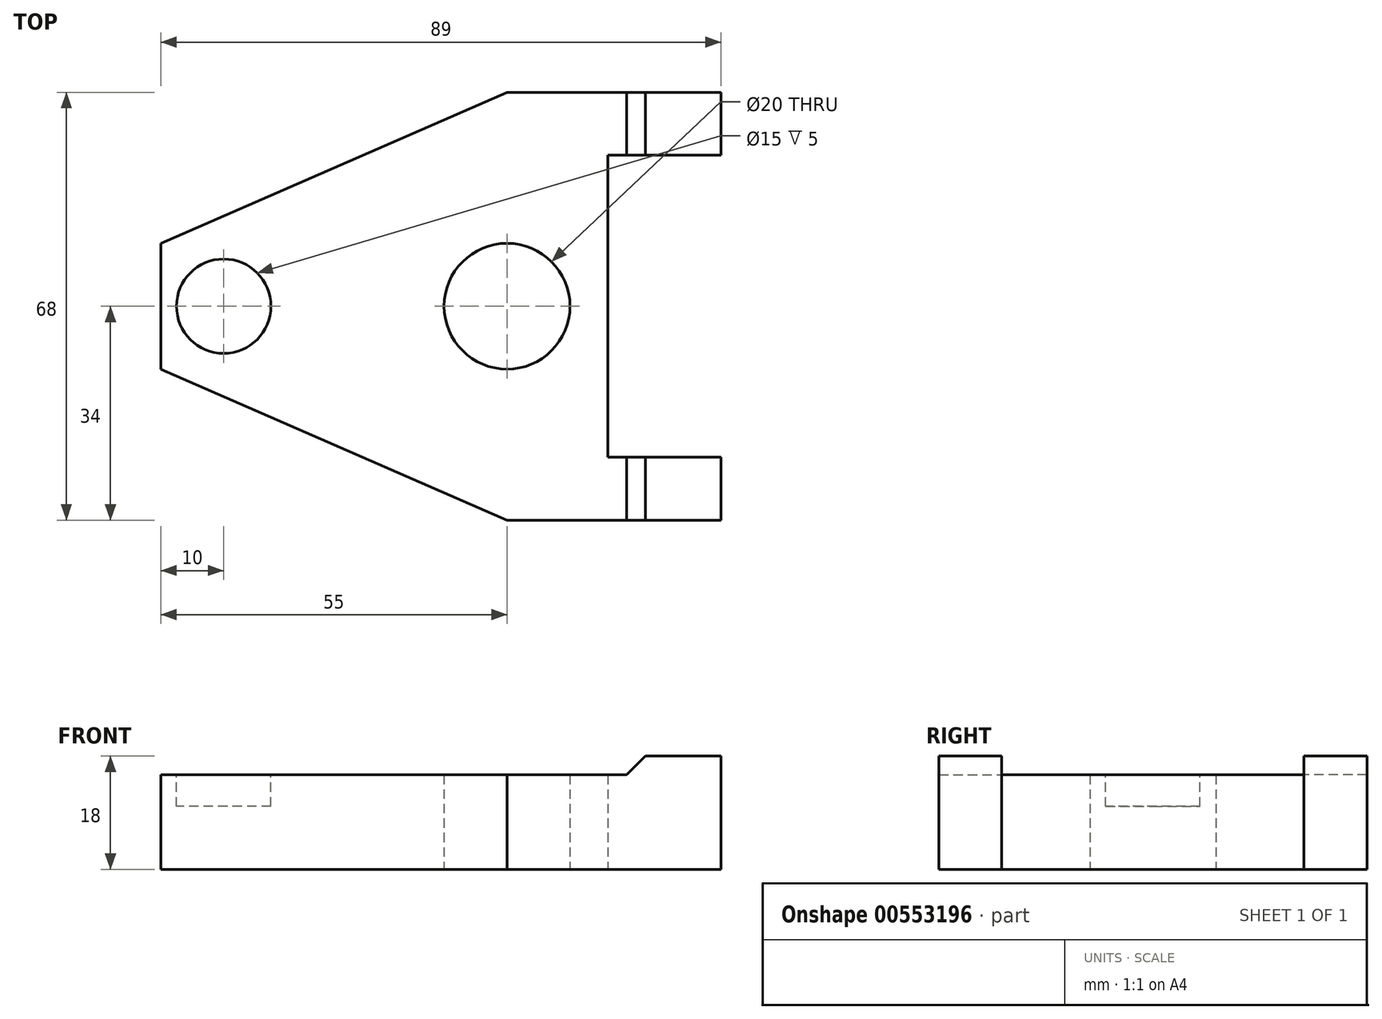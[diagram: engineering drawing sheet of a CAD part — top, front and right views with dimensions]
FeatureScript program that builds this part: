
annotation { "Feature Type Name" : "Feature", "Feature Type Description" : "" }
export const myFeature = defineFeature(function(context is Context, id is Id, definition is map)
    precondition{}
    {
        {
            var Q0;
            Q0=qCreatedBy(makeId("Front.planeOp"),FACE);
            var sketch = newSketch(context, id + "F0", { "sketchPlane" : qUnion([Q0])});
            skLineSegment(sketch, "E0", {"start": v(-55, 0) * mm, "end": v(-55, 15) * mm});
            skLineSegment(sketch, "E1", {"start": v(-55, 15) * mm, "end": v(19, 15) * mm});
            skLineSegment(sketch, "E2", {"start": v(19, 15) * mm, "end": v(22, 18) * mm});
            skLineSegment(sketch, "E3", {"start": v(22, 18) * mm, "end": v(34, 18) * mm});
            skLineSegment(sketch, "E4", {"start": v(34, 18) * mm, "end": v(34, 0) * mm});
            skLineSegment(sketch, "E5", {"start": v(34, 0) * mm, "end": v(-55, 0) * mm});
            skSolve(sketch);
        }
        {
            var Q0;
            Q0=qCreatedBy(makeId("Top.planeOp"),FACE);
            var sketch = newSketch(context, id + "F1", { "sketchPlane" : qUnion([Q0])});
            skLineSegment(sketch, "E6", {"start": v(-55, 0) * mm, "end": v(-55, -10) * mm});
            skLineSegment(sketch, "E7", {"start": v(-55, -10) * mm, "end": v(0, -34) * mm});
            skLineSegment(sketch, "E8", {"start": v(0, -34) * mm, "end": v(34, -34) * mm});
            skLineSegment(sketch, "E9", {"start": v(34, -34) * mm, "end": v(34, -24) * mm});
            skLineSegment(sketch, "E10", {"start": v(34, -24) * mm, "end": v(16, -24) * mm});
            skLineSegment(sketch, "E11", {"start": v(16, -24) * mm, "end": v(16, 0) * mm});
            skLineSegment(sketch, "E12", {"start": v(16, 0) * mm, "end": v(-55, 0) * mm});
            skSolve(sketch);
        }
        {
            var Q0;
            Q0=qCreatedBy(makeId("Top.planeOp"),FACE);
            var sketch = newSketch(context, id + "F2", { "sketchPlane" : qUnion([Q0])});
            skPoint(sketch, "E13", {"position": v(-45, 0) * mm});
            skPoint(sketch, "E14", {"position": v(0, 0) * mm});
            skSolve(sketch);
        }
        {
            var Q0;
            Q0=makeQuery(id+"F0.imprint","IMPRINT",FACE,{"disambiguationData":[TD([[makeQuery(id+"F0.imprint","IMPRINT",EDGE,{"derivedFrom":sQuery(id+"F0.wireOp",EDGE,"E0")}),-1.0]])]});
            extrude(context, id + "F3", {"entities" : qUnion([Q0]), "depth" : (68 / 2) * mm, "offsetDistance" : 25 * mm});
        }
        {
            var Q0;
            Q0 = qSketchRegion(id + "F1", true);
            extrude(context, id + "F4", {"entities" : qUnion([Q0]), "operationType" : NewBodyOperationType.INTERSECT, "endBound" : BoundingType.THROUGH_ALL, "depth" : 25 * mm, "offsetDistance" : 25 * mm});
        }
        {
            var Q0;
            Q0=makeQuery(id+"F3.opExtrude","SWEPT_BODY",BODY,{"disambiguationData":[OSD([sQuery(id+"F0.wireOp",EDGE,"E0"),sQuery(id+"F0.wireOp",EDGE,"E1"),sQuery(id+"F0.wireOp",EDGE,"E2"),sQuery(id+"F0.wireOp",EDGE,"E3"),sQuery(id+"F0.wireOp",EDGE,"E4"),sQuery(id+"F0.wireOp",EDGE,"E5")])]});
            var Q1;
            Q1=qCreatedBy(makeId("Front.planeOp"),FACE);
            mirror(context, id + "F5", {"operationType" : NewBodyOperationType.ADD, "entities" : qUnion([Q0]), "mirrorPlane" : qUnion([Q1])});
        }
        {
            var Q0;
            Q0=sQuery(id+"F2.wireOp",VERTEX,"E14");
            var Q1;
            Q1=makeQuery(id+"F3.opExtrude","SWEPT_BODY",BODY,{"disambiguationData":[OSD([sQuery(id+"F0.wireOp",EDGE,"E0"),sQuery(id+"F0.wireOp",EDGE,"E1"),sQuery(id+"F0.wireOp",EDGE,"E2"),sQuery(id+"F0.wireOp",EDGE,"E3"),sQuery(id+"F0.wireOp",EDGE,"E4"),sQuery(id+"F0.wireOp",EDGE,"E5")])]});
            hole(context, id + "F6", {"style" : HoleStyle.SIMPLE, "endStyle" : HoleEndStyle.THROUGH, "oppositeDirection" : true, "holeDiameter" : 20 * mm, "isTappedThrough" : true, "tappedDepth" : 12 * mm, "tapClearance" : 3, "locations" : qUnion([Q0]), "scope" : qUnion([Q1])});
        }
        {
            var Q0;
            {var subQ0=makeQuery(id+"F3.opExtrude","SWEPT_FACE",FACE,{"disambiguationData":[OSD([sQuery(id+"F0.wireOp",EDGE,"E1")])]});Q0=makeQuery(id+"F5.boolean.opBoolean","MERGE",FACE,{"derivedFrom":[subQ0,makeQuery(id+"F5.opPattern","COPY",FACE,{"derivedFrom":subQ0,"instanceName":"1"})]});}
            var sketch = newSketch(context, id + "F7", { "sketchPlane" : qUnion([Q0])});
            skCircle(sketch, "E15", {"center": v(-45, 0) * mm, "radius": 7.5 * mm});
            skSolve(sketch);
        }
        {
            var Q0;
            Q0=makeQuery(id+"F7.imprint","IMPRINT",FACE,{"disambiguationData":[TD([[makeQuery(id+"F7.imprint","IMPRINT",EDGE,{"derivedFrom":sQuery(id+"F7.wireOp",EDGE,"E15")}),1.0]])]});
            extrude(context, id + "F8", {"entities" : qUnion([Q0]), "operationType" : NewBodyOperationType.REMOVE, "oppositeDirection" : true, "depth" : 5 * mm, "offsetDistance" : 25 * mm});
        }
    });
